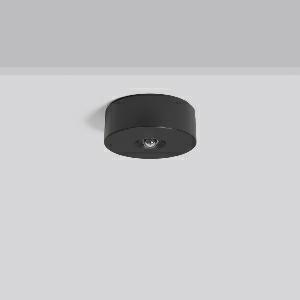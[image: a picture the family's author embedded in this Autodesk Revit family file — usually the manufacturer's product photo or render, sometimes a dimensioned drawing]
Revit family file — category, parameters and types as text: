
# Revit family: lucio_2_672527_003_04_53dd
name_source: partatom
category: Lighting Fixtures
units: mm (PartAtom-declared; Revit-internal decimal feet)

## family parameters
Cut with Voids When Loaded = No
Host = Face
Light Source = No
Part Type = Normal
Room Calculation Point = No
Round Connector Dimension = Use Diameter
Shared = No

## types (1)
- Flaechenlinse 3h (1 x LED Modul 740, 240 lm, 4000)
    Apparent Load = 0 VA
    CIE Flux Codes = 44 87 99 100 100
    Color Rendering = 70
    Color Temperature = 4000
    Default Elevation = 1800 mm
    Description = Series: LUCIO 2
Round surface-mounted downlight. For escape route illumination. Housing: plastic (polycarbonate). Cover: polycarbonate. Plastic lenses for area lighting and escape route illumination included in scope of delivery. Suitable for Ceiling mounting. Self-contained system with automatic self-test and feedback to the RZB monitoring system MULTIDIGIT. 
Colour: black
Diameter: 110 mm
Height: 46 mm
Weight: 0.29 kg
Operating mode: non-maintained power mode
Duration time: 3 h, 8 h
Lamp: LED
Socket: without socket
Colour temperature: 4000K
Colour rendering index (CRI): 70
Luminous flux, emergency: 240 lm
System power, emergency: -
Luminous flux, emergency 2: 220 lm
System power, emergency 2: -
Luminous flux, emergency 3: 120 lm
System power, emergency 3: -
Luminous flux, emergency 4: 110 lm
Control gear: EB in emergency mode only
Protection class: II
Type of protection: IP 20
    Height = 46 mm
    Lamp = 1 x LED Modul 740
    Lamp Light Flux = 240 lm
    Lamp count = 1
    Length = 110 mm
    Lifetime = 50000 h
    Luminous efficacy = 0 lm/W
    Manufacturer = RZB
    ModVariant = No
    Model = 672527.003.04
    Mounting Place = Ceiling
    Mounting Type = Surface mounted
    Number of Poles = 1
    OnlyDefault = Yes
    Power Factor = 1
    Product Name = LUCIO 2
    Product group = Surface mounted ceiling luminaires
    ProductGroupID = 303
    Protection Class = Protection class II
    Protection Degree = Degree of protection
    RLX_Detail_Level = 1
    RLX_Emergency_Light_Flux = 240 lm
    RLX_Emergency_Type = 3
    RLX_Emergency_Type_DB = Yes
    RlxData = <blob elided: 196837 chars, md5=bbac0346>
    Socket = socket
    Standby Power = 0 W
    System Light Flux = 0 lm
    System Power = 0 W
    Type Image = 672527.003.jpg
    URL = http://relux.com
    VarID = flaechenlinse_3h
    Voltage = 0 V
    Weight = 0.00 kg
    Width = 0 mm  [stored 0 ft]

note: [stored X ft] marks values corroborated as IEEE doubles in the binary element streams (Revit-internal decimal feet)

## geometry (parser evidence)
native form markers: Blend x4, Sweep x13
no freeform markers — native parametric forms only
